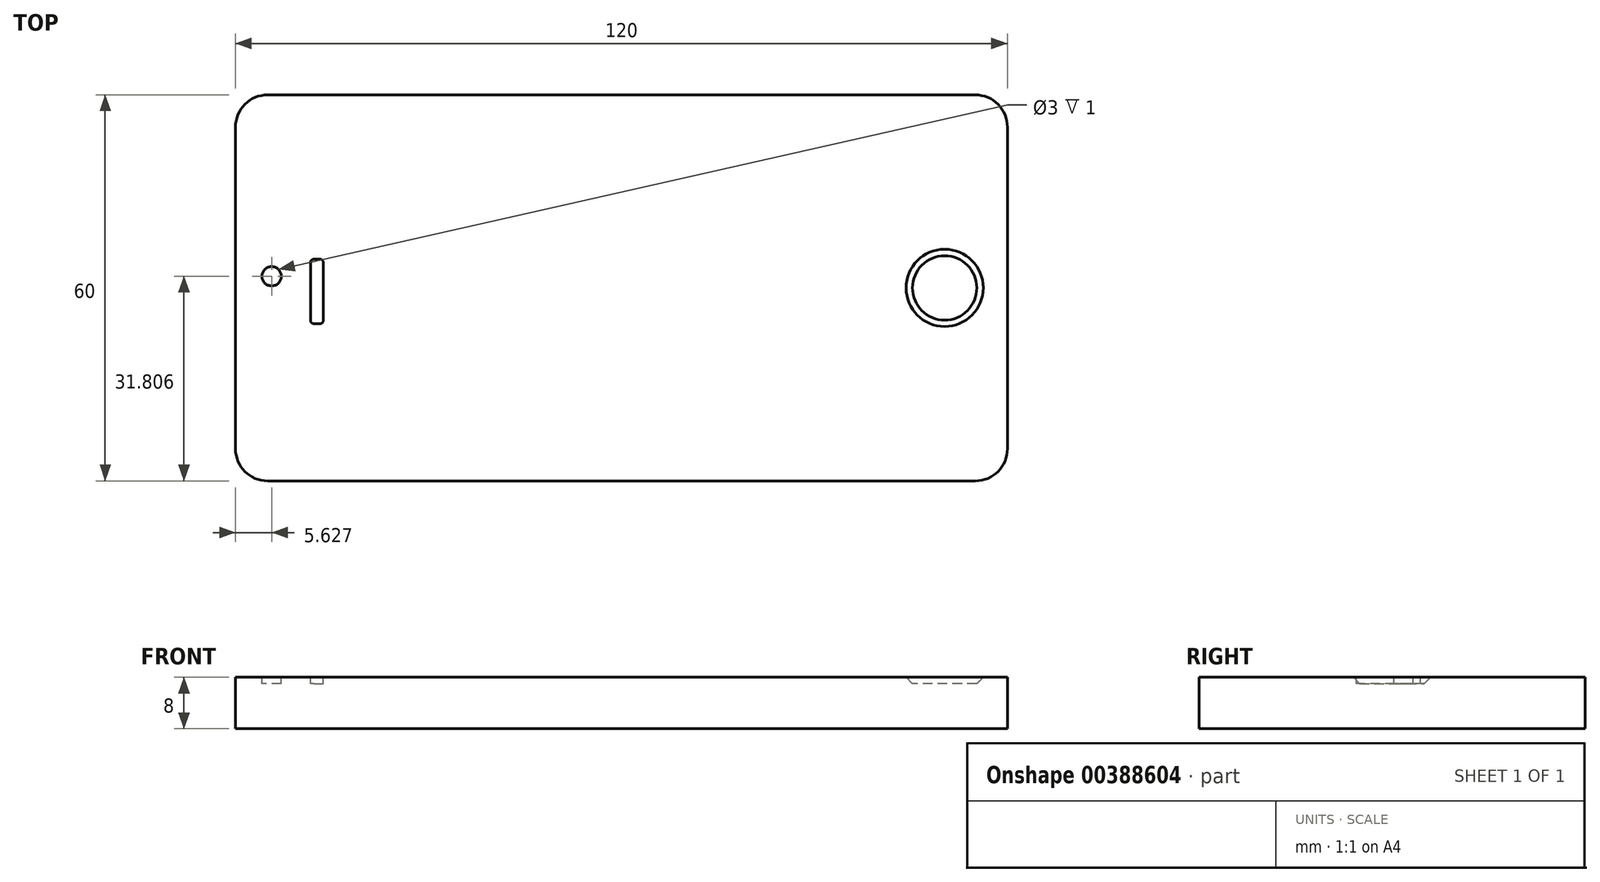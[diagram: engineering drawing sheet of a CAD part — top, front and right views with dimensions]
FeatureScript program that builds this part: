
annotation { "Feature Type Name" : "Feature", "Feature Type Description" : "" }
export const myFeature = defineFeature(function(context is Context, id is Id, definition is map)
    precondition{}
    {
        {
            var Q0;
            Q0=qCreatedBy(makeId("Top.planeOp"),FACE);
            var sketch = newSketch(context, id + "F0", { "sketchPlane" : qUnion([Q0])});
            skLineSegment(sketch, "E0.bottom", {"start": v(0, 0) * mm, "end": v(120, 0) * mm});
            skLineSegment(sketch, "E0.top", {"start": v(0, 60) * mm, "end": v(120, 60) * mm});
            skLineSegment(sketch, "E0.left", {"start": v(0, 0) * mm, "end": v(0, 60) * mm});
            skLineSegment(sketch, "E0.right", {"start": v(120, 0) * mm, "end": v(120, 60) * mm});
            skSolve(sketch);
        }
        {
            var Q0;
            Q0 = qSketchRegion(id + "F0", true);
            extrude(context, id + "F1", {"entities" : qUnion([Q0]), "depth" : 8 * mm});
        }
        {
            var Q0;
            Q0=makeQuery(id+"F1.opExtrude","SWEPT_EDGE",EDGE,{"disambiguationData":[OSD([sQuery(id+"F0.wireOp",EDGE,"E0.top"),sQuery(id+"F0.wireOp",EDGE,"E0.left")])]});
            fillet(context, id + "F2", {"entities" : qUnion([Q0]), "radius" : 5 * mm, "tangentPropagation" : true, "allowEdgeOverflow" : false});
        }
        {
            var Q0;
            Q0=makeQuery(id+"F1.opExtrude","SWEPT_EDGE",EDGE,{"disambiguationData":[OSD([sQuery(id+"F0.wireOp",EDGE,"E0.bottom"),sQuery(id+"F0.wireOp",EDGE,"E0.left")])]});
            fillet(context, id + "F3", {"entities" : qUnion([Q0]), "radius" : 5 * mm, "tangentPropagation" : true, "allowEdgeOverflow" : false});
        }
        {
            var Q0;
            Q0=makeQuery(id+"F1.opExtrude","SWEPT_EDGE",EDGE,{"disambiguationData":[OSD([sQuery(id+"F0.wireOp",EDGE,"E0.bottom"),sQuery(id+"F0.wireOp",EDGE,"E0.right")])]});
            fillet(context, id + "F4", {"entities" : qUnion([Q0]), "radius" : 5 * mm, "tangentPropagation" : true, "allowEdgeOverflow" : false});
        }
        {
            var Q0;
            Q0=makeQuery(id+"F1.opExtrude","SWEPT_EDGE",EDGE,{"disambiguationData":[OSD([sQuery(id+"F0.wireOp",EDGE,"E0.top"),sQuery(id+"F0.wireOp",EDGE,"E0.right")])]});
            fillet(context, id + "F5", {"entities" : qUnion([Q0]), "radius" : 5 * mm, "tangentPropagation" : true, "allowEdgeOverflow" : false});
        }
        {
            var Q0;
            Q0=makeQuery(id+"F1.opExtrude","CAP_FACE",FACE,{"disambiguationData":[OSD([sQuery(id+"F0.wireOp",EDGE,"E0.bottom"),sQuery(id+"F0.wireOp",EDGE,"E0.top"),sQuery(id+"F0.wireOp",EDGE,"E0.left"),sQuery(id+"F0.wireOp",EDGE,"E0.right")])],"isStart":false});
            var sketch = newSketch(context, id + "F6", { "sketchPlane" : qUnion([Q0])});
            skLineSegment(sketch, "E1.bottom", {"start": v(11.66, 24.45) * mm, "end": v(13.66, 24.45) * mm});
            skLineSegment(sketch, "E1.top", {"start": v(11.66, 34.45) * mm, "end": v(13.66, 34.45) * mm});
            skLineSegment(sketch, "E1.left", {"start": v(11.66, 24.45) * mm, "end": v(11.66, 34.45) * mm});
            skLineSegment(sketch, "E1.right", {"start": v(13.66, 24.45) * mm, "end": v(13.66, 34.45) * mm});
            skSolve(sketch);
        }
        {
            var Q0;
            Q0 = qSketchRegion(id + "F6", true);
            extrude(context, id + "F7", {"entities" : qUnion([Q0]), "operationType" : NewBodyOperationType.REMOVE, "oppositeDirection" : true, "depth" : 1 * mm});
        }
        {
            var Q0;
            Q0=makeQuery(id+"F7.boolean.opBoolean","COPY",EDGE,{"derivedFrom":makeQuery(id+"F7.opExtrude","SWEPT_EDGE",EDGE,{"disambiguationData":[OSD([sQuery(id+"F6.wireOp",EDGE,"E1.bottom"),sQuery(id+"F6.wireOp",EDGE,"E1.left")])]})});
            var Q1;
            Q1=makeQuery(id+"F7.boolean.opBoolean","COPY",EDGE,{"derivedFrom":makeQuery(id+"F7.opExtrude","SWEPT_EDGE",EDGE,{"disambiguationData":[OSD([sQuery(id+"F6.wireOp",EDGE,"E1.bottom"),sQuery(id+"F6.wireOp",EDGE,"E1.right")])]})});
            fillet(context, id + "F8", {"entities" : qUnion([Q0, Q1]), "radius" : 0.5 * mm, "tangentPropagation" : true, "allowEdgeOverflow" : false});
        }
        {
            var Q0;
            Q0=makeQuery(id+"F7.boolean.opBoolean","COPY",EDGE,{"derivedFrom":makeQuery(id+"F7.opExtrude","SWEPT_EDGE",EDGE,{"disambiguationData":[OSD([sQuery(id+"F6.wireOp",EDGE,"E1.top"),sQuery(id+"F6.wireOp",EDGE,"E1.right")])]})});
            var Q1;
            Q1=makeQuery(id+"F7.boolean.opBoolean","COPY",EDGE,{"derivedFrom":makeQuery(id+"F7.opExtrude","SWEPT_EDGE",EDGE,{"disambiguationData":[OSD([sQuery(id+"F6.wireOp",EDGE,"E1.top"),sQuery(id+"F6.wireOp",EDGE,"E1.left")])]})});
            fillet(context, id + "F9", {"entities" : qUnion([Q0, Q1]), "radius" : 0.5 * mm, "tangentPropagation" : true, "allowEdgeOverflow" : false});
        }
        {
            var Q0;
            Q0=makeQuery(id+"F1.opExtrude","CAP_FACE",FACE,{"disambiguationData":[OSD([sQuery(id+"F0.wireOp",EDGE,"E0.bottom"),sQuery(id+"F0.wireOp",EDGE,"E0.top"),sQuery(id+"F0.wireOp",EDGE,"E0.left"),sQuery(id+"F0.wireOp",EDGE,"E0.right")])],"isStart":false});
            var sketch = newSketch(context, id + "F10", { "sketchPlane" : qUnion([Q0])});
            skCircle(sketch, "E2", {"center": v(5.63, 31.8) * mm, "radius": 1.5 * mm});
            skSolve(sketch);
        }
        {
            var Q0;
            Q0 = qSketchRegion(id + "F10", true);
            extrude(context, id + "F11", {"entities" : qUnion([Q0]), "operationType" : NewBodyOperationType.REMOVE, "oppositeDirection" : true, "depth" : 1 * mm});
        }
        {
            var Q0;
            Q0=makeQuery(id+"F1.opExtrude","CAP_FACE",FACE,{"disambiguationData":[OSD([sQuery(id+"F0.wireOp",EDGE,"E0.bottom"),sQuery(id+"F0.wireOp",EDGE,"E0.top"),sQuery(id+"F0.wireOp",EDGE,"E0.left"),sQuery(id+"F0.wireOp",EDGE,"E0.right")])],"isStart":false});
            var sketch = newSketch(context, id + "F12", { "sketchPlane" : qUnion([Q0])});
            skCircle(sketch, "E3", {"center": v(5.63, 31.8) * mm, "radius": 0.78 * mm});
            skSolve(sketch);
        }
        {
            var Q0;
            {var subQ1=sQuery(id+"F0.wireOp",EDGE,"E0.left");Q0=makeQuery(id+"F12.imprint","IMPRINT",FACE,{"disambiguationData":[TD([[makeQuery(id+"F12.imprint","IMPRINT",EDGE,{"derivedFrom":makeQuery(id+"F1.opExtrude","CAP_EDGE",EDGE,{"disambiguationData":[OSD([subQ1])],"isStart":false})}),-1.0]])]});}
            var sketch = newSketch(context, id + "F13", { "sketchPlane" : qUnion([Q0])});
            skLineSegment(sketch, "E4.bottom", {"start": v(20, 3) * mm, "end": v(100, 3) * mm});
            skLineSegment(sketch, "E4.top", {"start": v(20, 57) * mm, "end": v(100, 57) * mm});
            skLineSegment(sketch, "E4.left", {"start": v(20, 3) * mm, "end": v(20, 57) * mm});
            skLineSegment(sketch, "E4.right", {"start": v(100, 3) * mm, "end": v(100, 57) * mm});
            skSolve(sketch);
        }
        {
            var Q0;
            Q0=makeQuery(id+"F13.imprint","IMPRINT",FACE,{"disambiguationData":[TD([[makeQuery(id+"F13.imprint","IMPRINT",EDGE,{"derivedFrom":sQuery(id+"F13.wireOp",EDGE,"E4.bottom")}),-1.0]])]});
            var sketch = newSketch(context, id + "F14", { "sketchPlane" : qUnion([Q0])});
            skCircle(sketch, "E5", {"center": v(110.24, 30) * mm, "radius": 6 * mm});
            skSolve(sketch);
        }
        {
            var Q0;
            Q0 = qSketchRegion(id + "F14", true);
            extrude(context, id + "F15", {"entities" : qUnion([Q0]), "operationType" : NewBodyOperationType.REMOVE, "oppositeDirection" : true, "depth" : 1 * mm});
        }
        {
            var Q0;
            Q0=makeQuery(id+"F15.boolean.opBoolean","COPY",EDGE,{"derivedFrom":makeQuery(id+"F15.opExtrude","CAP_EDGE",EDGE,{"disambiguationData":[OSD([sQuery(id+"F14.wireOp",EDGE,"E5")])],"isStart":false})});
            chamfer(context, id + "F16", {"entities" : qUnion([Q0]), "width" : 1 * mm, "tangentPropagation" : true});
        }
    });
